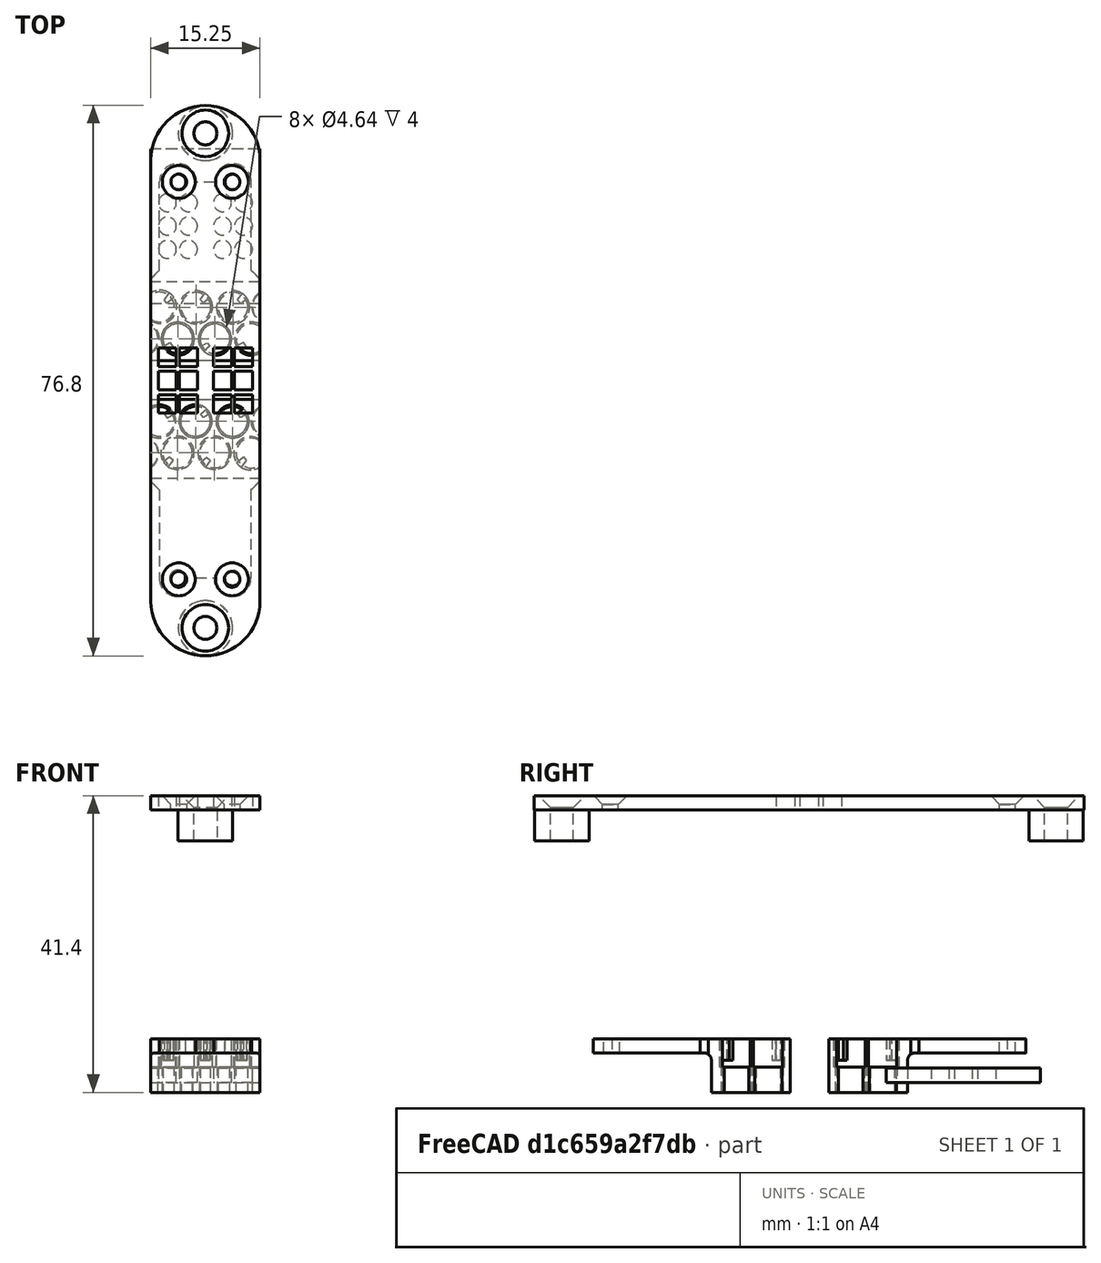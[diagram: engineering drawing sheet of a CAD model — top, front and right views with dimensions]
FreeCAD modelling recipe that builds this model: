
FCSTD DOCUMENT  (FreeCAD 0.16R6706 (Git))
Label: BrailleCell_ExplodedView
License: All rights reserved
LicenseURL: http://en.wikipedia.org/wiki/All_rights_reserved
objects: Sketcher::SketchObject×11, PartDesign::Pad×11, PartDesign::Chamfer×5, Part::MultiFuse×5, Mesh::Feature×4, Part::Box×2, Part::Cut×2, PartDesign::Fillet×2
note: 49 computed .brp shape members not serialized (recipe doc carries the construction recipe); baked Part::Feature solids carry a one-line shape summary decoded from their .brp

FEATURE [Sketcher::SketchObject] Sketch001
  sketch-geometry (12):
    g0: LineSegment StartX=0 StartY=0 StartZ=0 EndX=15.232 EndY=0 EndZ=0
    g1: LineSegment StartX=15.232 StartY=0 StartZ=0 EndX=15.232 EndY=-20 EndZ=0
    g2: LineSegment StartX=15.232 StartY=-20 StartZ=0 EndX=0 EndY=-20 EndZ=0
    g3: LineSegment StartX=0 StartY=-20 StartZ=0 EndX=0 EndY=0 EndZ=0
    g4: Circle CenterX=3.8995 CenterY=-16.9419 CenterZ=0 NormalX=0 NormalY=0 NormalZ=1 Radius=1.1
    g5: Circle CenterX=11.3325 CenterY=-16.9419 CenterZ=0 NormalX=0 NormalY=0 NormalZ=1 Radius=1.1
    g6: LineSegment StartX=0 StartY=21.56 StartZ=0 EndX=15.232 EndY=21.56 EndZ=0
    g7: LineSegment StartX=15.232 StartY=21.56 StartZ=0 EndX=15.232 EndY=41.56 EndZ=0
    g8: LineSegment StartX=15.232 StartY=41.56 StartZ=0 EndX=0 EndY=41.56 EndZ=0
    g9: LineSegment StartX=0 StartY=41.56 StartZ=0 EndX=0 EndY=21.56 EndZ=0
    g10: Circle CenterX=3.8995 CenterY=38.5019 CenterZ=0 NormalX=0 NormalY=0 NormalZ=1 Radius=1.1
    g11: Circle CenterX=11.3325 CenterY=38.5019 CenterZ=0 NormalX=0 NormalY=0 NormalZ=1 Radius=1.1
  constraints (34):
    c: Coincident(g0,g1)
    c: Coincident(g1,g2)
    c: Coincident(g2,g3)
    c: Coincident(g3,g0)
    c: Horizontal(g0)
    c: Horizontal(g2)
    c: Vertical(g1)
    c: Vertical(g3)
    c: DistanceX(g-1,g0) = 15.232
    c: DistanceY(g2,g-1) = 20
    c: DistanceY(g4,g-1) = 16.9419
    c: Radius(g4) = 1.1
    c: DistanceY(g5,g-1) = 16.9419
    c: Radius(g5) = 1.1
    c: Coincident(g6,g7)
    c: Coincident(g7,g8)
    c: Coincident(g8,g9)
    c: Coincident(g9,g6)
    c: Horizontal(g6)
    c: Horizontal(g8)
    c: Vertical(g7)
    c: Vertical(g9)
    c: PointOnObject(g6,g-2)
    c: DistanceX(g6,g6) = 15.232
    c: DistanceY(g6,g7) = 20
    c: Radius(g11) = 1.1
    c: Radius(g10) = 1.1
    c: DistanceY(g-1,g10) = 38.5019
    c: DistanceY(g-1,g11) = 38.5019
    c: DistanceX(g6,g10) = 3.8995
    c: DistanceX(g-1,g11) = 11.3325
    c: DistanceX(g-1,g4) = 3.8995
    c: DistanceX(g-1,g5) = 11.3325
    c: DistanceY(g-1,g6) = 21.56
FEATURE [Sketcher::SketchObject] Sketch002
  sketch-geometry (6):
    g0: ArcOfCircle CenterX=7.616 CenterY=41.56 CenterZ=0 NormalX=0 NormalY=0 NormalZ=1 Radius=7.616 StartAngle=0 EndAngle=3.14159
    g1: ArcOfCircle CenterX=7.616 CenterY=-20 CenterZ=0 NormalX=0 NormalY=0 NormalZ=1 Radius=7.616 StartAngle=3.14159 EndAngle=6.28319
    g2: Circle CenterX=7.616 CenterY=45.28 CenterZ=0 NormalX=0 NormalY=0 NormalZ=1 Radius=1.6
    g3: Circle CenterX=7.616 CenterY=-23.72 CenterZ=0 NormalX=0 NormalY=0 NormalZ=1 Radius=1.6
    g4: LineSegment StartX=0 StartY=-20 StartZ=0 EndX=15.232 EndY=-20 EndZ=0
    g5: LineSegment StartX=0 StartY=41.56 StartZ=0 EndX=15.232 EndY=41.56 EndZ=0
  constraints (20):
    c: DistanceY(g-1,g0) = 41.56
    c: DistanceY(g-1,g0) = 41.56
    c: DistanceY(g-1,g0) = 41.56
    c: DistanceX(g-1,g0) = 7.616
    c: DistanceY(g1,g-1) = 20
    c: DistanceX(g-1,g1) = 7.616
    c: Radius(g2) = 1.6
    c: DistanceY(g-1,g2) = 45.28
    c: DistanceX(g-1,g2) = 7.616
    c: DistanceX(g1,g3) = 7.616
    c: Radius(g3) = 1.6
    c: DistanceY(g3,g-1) = 23.72
    c: Coincident(g4,g1)
    c: Coincident(g4,g1)
    c: Horizontal(g4)
    c: Coincident(g5,g0)
    c: Coincident(g5,g0)
    c: DistanceX(g-1,g0) = 0
    c: DistanceX(g-1,g1) = 0
    c: DistanceY(g1,g1) = 0
FEATURE [PartDesign::Pad] Pad
  Length = 2
  Length2 = 100
  Sketch = -> Sketch002
  Type = 0
FEATURE [PartDesign::Pad] Pad001
  Length = 2
  Length2 = 100
  Sketch = -> Sketch001
  Type = 0
FEATURE [Sketcher::SketchObject] Sketch004
  sketch-geometry (16):
    g0: LineSegment StartX=0 StartY=0 StartZ=0 EndX=15.232 EndY=0 EndZ=0
    g1: LineSegment StartX=15.232 StartY=0 StartZ=0 EndX=15.232 EndY=21.56 EndZ=0
    g2: LineSegment StartX=15.232 StartY=21.56 StartZ=0 EndX=0 EndY=21.56 EndZ=0
    g3: LineSegment StartX=0 StartY=21.56 StartZ=0 EndX=0 EndY=0 EndZ=0
    g4: Circle CenterX=2.3099 CenterY=7.53 CenterZ=0 NormalX=0 NormalY=0 NormalZ=1 Radius=1.25
    g5: Circle CenterX=2.3099 CenterY=14.03 CenterZ=0 NormalX=0 NormalY=0 NormalZ=1 Radius=1.25
    g6: Circle CenterX=2.3099 CenterY=10.78 CenterZ=0 NormalX=0 NormalY=0 NormalZ=1 Radius=1.25
    g7: Circle CenterX=5.2399 CenterY=14.03 CenterZ=0 NormalX=0 NormalY=0 NormalZ=1 Radius=1.25
    g8: Circle CenterX=5.2399 CenterY=10.78 CenterZ=0 NormalX=0 NormalY=0 NormalZ=1 Radius=1.25
    g9: Circle CenterX=5.2399 CenterY=7.53 CenterZ=0 NormalX=0 NormalY=0 NormalZ=1 Radius=1.25
    g10: Circle CenterX=10 CenterY=14.03 CenterZ=0 NormalX=0 NormalY=0 NormalZ=1 Radius=1.25
    g11: Circle CenterX=10 CenterY=10.78 CenterZ=0 NormalX=0 NormalY=0 NormalZ=1 Radius=1.25
    g12: Circle CenterX=10 CenterY=7.53 CenterZ=0 NormalX=0 NormalY=0 NormalZ=1 Radius=1.25
    g13: Circle CenterX=12.93 CenterY=7.53 CenterZ=0 NormalX=0 NormalY=0 NormalZ=1 Radius=1.25
    g14: Circle CenterX=12.93 CenterY=10.78 CenterZ=0 NormalX=0 NormalY=0 NormalZ=1 Radius=1.25
    g15: Circle CenterX=12.93 CenterY=14.03 CenterZ=0 NormalX=0 NormalY=0 NormalZ=1 Radius=1.25
  constraints (47):
    c: Coincident(g0,g1)
    c: Coincident(g1,g2)
    c: Coincident(g2,g3)
    c: Coincident(g3,g0)
    c: Horizontal(g0)
    c: Horizontal(g2)
    c: Vertical(g1)
    c: Vertical(g3)
    c: Coincident(g0,g-1)
    c: DistanceX(g-1,g0) = 15.232
    c: DistanceY(g-1,g2) = 21.56
    c: DistanceX(g3,g4) = 2.3099
    c: Radius(g4) = 1.25
    c: DistanceY(g4,g6) = 3.25
    c: Radius(g6) = 1.25
    c: DistanceX(g4,g6) = 0
    c: DistanceX(g6,g5) = 0
    c: Radius(g5) = 1.25
    c: DistanceY(g6,g5) = 3.25
    c: DistanceY(g3,g6) = -10.78
    c: Radius(g9) = 1.25
    c: Radius(g8) = 1.25
    c: Radius(g7) = 1.25
    c: DistanceX(g8,g9) = 0
    c: DistanceX(g7,g8) = 0
    c: DistanceY(g8,g7) = 3.25
    c: DistanceY(g9,g8) = 3.25
    c: DistanceX(g4,g9) = 2.93
    c: DistanceY(g6,g8) = 0
    c: Radius(g15) = 1.25
    c: Radius(g10) = 1.25
    c: Radius(g11) = 1.25
    c: Radius(g14) = 1.25
    c: Radius(g12) = 1.25
    c: Radius(g13) = 1.25
    c: DistanceX(g13,g14) = 0
    c: DistanceX(g15,g14) = 0
    c: DistanceY(g14,g15) = 3.25
    c: DistanceY(g13,g14) = 3.25
    c: DistanceX(g12,g11) = 0
    c: DistanceX(g11,g10) = 0
    c: DistanceY(g11,g10) = 3.25
    c: DistanceY(g12,g11) = 3.25
    c: DistanceY(g13,g12) = 0
    c: DistanceY(g3,g11) = -10.78
    c: DistanceX(g3,g11) = 10
    c: DistanceX(g11,g14) = 2.93
FEATURE [PartDesign::Pad] Pad002
  Length = 2
  Length2 = 100
  Sketch = -> Sketch004
  Type = 0
FEATURE [PartDesign::Chamfer] Chamfer
  Base = -> Pad [Edge8]
  Size = 1.65
FEATURE [PartDesign::Chamfer] Chamfer002
  Base = -> Pad001 [Edge35,Edge32,Edge17,Edge14]
  Size = 1.2
FEATURE [PartDesign::Chamfer] Chamfer003
  Base = -> Chamfer [Edge19]
  Size = 1.65
FEATURE [Sketcher::SketchObject] Sketch005
  sketch-geometry (52):
    g0: LineSegment StartX=0 StartY=0 StartZ=0 EndX=15.232 EndY=0 EndZ=0
    g1: LineSegment StartX=15.232 StartY=0 StartZ=0 EndX=15.232 EndY=21.56 EndZ=0
    g2: LineSegment StartX=15.232 StartY=21.56 StartZ=0 EndX=0 EndY=21.56 EndZ=0
    g3: LineSegment StartX=0 StartY=21.56 StartZ=0 EndX=0 EndY=0 EndZ=0
    g4: LineSegment StartX=1.0599 StartY=12.08 StartZ=0 EndX=3.5599 EndY=12.08 EndZ=0
    g5: LineSegment StartX=3.5599 StartY=12.08 StartZ=0 EndX=3.5599 EndY=9.48 EndZ=0
    g6: LineSegment StartX=3.5599 StartY=9.48 StartZ=0 EndX=1.0599 EndY=9.48 EndZ=0
    g7: LineSegment StartX=1.0599 StartY=9.48 StartZ=0 EndX=1.0599 EndY=12.08 EndZ=0
    g8: LineSegment StartX=1.0599 StartY=15.33 StartZ=0 EndX=3.5599 EndY=15.33 EndZ=0
    g9: LineSegment StartX=3.5599 StartY=15.33 StartZ=0 EndX=3.5599 EndY=12.73 EndZ=0
    g10: LineSegment StartX=3.5599 StartY=12.73 StartZ=0 EndX=1.0599 EndY=12.73 EndZ=0
    g11: LineSegment StartX=1.0599 StartY=12.73 StartZ=0 EndX=1.0599 EndY=15.33 EndZ=0
    g12: LineSegment StartX=1.0599 StartY=8.83 StartZ=0 EndX=3.5599 EndY=8.83 EndZ=0
    g13: LineSegment StartX=3.5599 StartY=8.83 StartZ=0 EndX=3.5599 EndY=6.23 EndZ=0
    g14: LineSegment StartX=3.5599 StartY=6.23 StartZ=0 EndX=1.0599 EndY=6.23 EndZ=0
    g15: LineSegment StartX=1.0599 StartY=6.23 StartZ=0 EndX=1.0599 EndY=8.83 EndZ=0
    g16: LineSegment StartX=3.9899 StartY=15.33 StartZ=0 EndX=6.4899 EndY=15.33 EndZ=0
    g17: LineSegment StartX=6.4899 StartY=15.33 StartZ=0 EndX=6.4899 EndY=12.73 EndZ=0
    g18: LineSegment StartX=6.4899 StartY=12.73 StartZ=0 EndX=3.9899 EndY=12.73 EndZ=0
    g19: LineSegment StartX=3.9899 StartY=12.73 StartZ=0 EndX=3.9899 EndY=15.33 EndZ=0
    g20: LineSegment StartX=3.9899 StartY=12.08 StartZ=0 EndX=6.4899 EndY=12.08 EndZ=0
    g21: LineSegment StartX=6.4899 StartY=12.08 StartZ=0 EndX=6.4899 EndY=9.48 EndZ=0
    g22: LineSegment StartX=6.4899 StartY=9.48 StartZ=0 EndX=3.9899 EndY=9.48 EndZ=0
    g23: LineSegment StartX=3.9899 StartY=9.48 StartZ=0 EndX=3.9899 EndY=12.08 EndZ=0
    g24: LineSegment StartX=3.9899 StartY=8.83 StartZ=0 EndX=6.4899 EndY=8.83 EndZ=0
    g25: LineSegment StartX=6.4899 StartY=8.83 StartZ=0 EndX=6.4899 EndY=6.23 EndZ=0
    g26: LineSegment StartX=6.4899 StartY=6.23 StartZ=0 EndX=3.9899 EndY=6.23 EndZ=0
    g27: LineSegment StartX=3.9899 StartY=6.23 StartZ=0 EndX=3.9899 EndY=8.83 EndZ=0
    g28: LineSegment StartX=8.75 StartY=15.33 StartZ=0 EndX=11.25 EndY=15.33 EndZ=0
    g29: LineSegment StartX=11.25 StartY=15.33 StartZ=0 EndX=11.25 EndY=12.73 EndZ=0
    g30: LineSegment StartX=11.25 StartY=12.73 StartZ=0 EndX=8.75 EndY=12.73 EndZ=0
    g31: LineSegment StartX=8.75 StartY=12.73 StartZ=0 EndX=8.75 EndY=15.33 EndZ=0
    g32: LineSegment StartX=11.68 StartY=15.33 StartZ=0 EndX=14.18 EndY=15.33 EndZ=0
    g33: LineSegment StartX=14.18 StartY=15.33 StartZ=0 EndX=14.18 EndY=12.73 EndZ=0
    g34: LineSegment StartX=14.18 StartY=12.73 StartZ=0 EndX=11.68 EndY=12.73 EndZ=0
    g35: LineSegment StartX=11.68 StartY=12.73 StartZ=0 EndX=11.68 EndY=15.33 EndZ=0
    g36: LineSegment StartX=8.75 StartY=12.08 StartZ=0 EndX=11.25 EndY=12.08 EndZ=0
    g37: LineSegment StartX=11.25 StartY=12.08 StartZ=0 EndX=11.25 EndY=9.48 EndZ=0
    g38: LineSegment StartX=11.25 StartY=9.48 StartZ=0 EndX=8.75 EndY=9.48 EndZ=0
    g39: LineSegment StartX=8.75 StartY=9.48 StartZ=0 EndX=8.75 EndY=12.08 EndZ=0
    g40: LineSegment StartX=11.68 StartY=12.08 StartZ=0 EndX=14.18 EndY=12.08 EndZ=0
    g41: LineSegment StartX=14.18 StartY=12.08 StartZ=0 EndX=14.18 EndY=9.48 EndZ=0
    g42: LineSegment StartX=14.18 StartY=9.48 StartZ=0 EndX=11.68 EndY=9.48 EndZ=0
    g43: LineSegment StartX=11.68 StartY=9.48 StartZ=0 EndX=11.68 EndY=12.08 EndZ=0
    g44: LineSegment StartX=8.75 StartY=8.83 StartZ=0 EndX=11.25 EndY=8.83 EndZ=0
    g45: LineSegment StartX=11.25 StartY=8.83 StartZ=0 EndX=11.25 EndY=6.23 EndZ=0
    g46: LineSegment StartX=11.25 StartY=6.23 StartZ=0 EndX=8.75 EndY=6.23 EndZ=0
    g47: LineSegment StartX=8.75 StartY=6.23 StartZ=0 EndX=8.75 EndY=8.83 EndZ=0
    g48: LineSegment StartX=11.68 StartY=8.83 StartZ=0 EndX=14.18 EndY=8.83 EndZ=0
    g49: LineSegment StartX=14.18 StartY=8.83 StartZ=0 EndX=14.18 EndY=6.23 EndZ=0
    g50: LineSegment StartX=14.18 StartY=6.23 StartZ=0 EndX=11.68 EndY=6.23 EndZ=0
    g51: LineSegment StartX=11.68 StartY=6.23 StartZ=0 EndX=11.68 EndY=8.83 EndZ=0
  constraints (155):
    c: Coincident(g0,g1)
    c: Coincident(g1,g2)
    c: Coincident(g2,g3)
    c: Coincident(g3,g0)
    c: Horizontal(g0)
    c: Horizontal(g2)
    c: Vertical(g1)
    c: Vertical(g3)
    c: Coincident(g0,g-1)
    c: DistanceX(g-1,g0) = 15.232
    c: DistanceY(g-1,g2) = 21.56
    c: Coincident(g4,g5)
    c: Coincident(g5,g6)
    c: Coincident(g6,g7)
    c: Coincident(g7,g4)
    c: Horizontal(g4)
    c: Horizontal(g6)
    c: Vertical(g5)
    c: Vertical(g7)
    c: Coincident(g8,g9)
    c: Coincident(g9,g10)
    c: Coincident(g10,g11)
    c: Coincident(g11,g8)
    c: Horizontal(g8)
    c: Horizontal(g10)
    c: Vertical(g9)
    c: Vertical(g11)
    c: Coincident(g12,g13)
    c: Coincident(g13,g14)
    c: Coincident(g14,g15)
    c: Coincident(g15,g12)
    c: Horizontal(g12)
    c: Horizontal(g14)
    c: Vertical(g13)
    c: Vertical(g15)
    c: Coincident(g16,g17)
    c: Coincident(g17,g18)
    c: Coincident(g18,g19)
    c: Coincident(g19,g16)
    c: Horizontal(g16)
    c: Horizontal(g18)
    c: Vertical(g17)
    c: Vertical(g19)
    c: Coincident(g20,g21)
    c: Coincident(g21,g22)
    c: Coincident(g22,g23)
    c: Coincident(g23,g20)
    c: Horizontal(g20)
    c: Horizontal(g22)
    c: Vertical(g21)
    c: Vertical(g23)
    c: Coincident(g24,g25)
    c: Coincident(g25,g26)
    c: Coincident(g26,g27)
    c: Coincident(g27,g24)
    c: Horizontal(g24)
    c: Horizontal(g26)
    c: Vertical(g25)
    c: Vertical(g27)
    c: DistanceY(g6,g4) = 2.6
    c: DistanceY(g10,g8) = 2.6
    c: DistanceY(g14,g12) = 2.6
    c: DistanceY(g-1,g6) = 9.48
    c: DistanceY(g22,g20) = 2.6
    c: DistanceY(g18,g16) = 2.6
    c: DistanceY(g26,g24) = 2.6
    c: DistanceY(g4,g10) = 0.65
    c: DistanceY(g12,g6) = 0.65
    c: DistanceY(g24,g22) = 0.65
    c: DistanceY(g20,g18) = 0.65
    c: DistanceX(g6,g5) = 2.5
    c: DistanceX(g14,g13) = 2.5
    c: DistanceX(g10,g4) = 0
    c: DistanceX(g6,g12) = 0
    c: DistanceX(g10,g9) = 2.5
    c: DistanceX(g20,g18) = 0
    c: DistanceX(g22,g24) = 0
    c: DistanceX(g22,g21) = 2.5
    c: DistanceX(g26,g25) = 2.5
    c: DistanceX(g18,g17) = 2.5
    c: DistanceX(g5,g22) = 0.43
    c: DistanceX(g-1,g6) = 1.0599
    c: Coincident(g28,g29)
    c: Coincident(g29,g30)
    c: Coincident(g30,g31)
    c: Coincident(g31,g28)
    c: Horizontal(g28)
    c: Horizontal(g30)
    c: Vertical(g29)
    c: Vertical(g31)
    c: Coincident(g32,g33)
    c: Coincident(g33,g34)
    c: Coincident(g34,g35)
    c: Coincident(g35,g32)
    c: Horizontal(g32)
    c: Horizontal(g34)
    c: Vertical(g33)
    c: Vertical(g35)
    c: Coincident(g36,g37)
    c: Coincident(g37,g38)
    c: Coincident(g38,g39)
    c: Coincident(g39,g36)
    c: Horizontal(g36)
    c: Horizontal(g38)
    c: Vertical(g37)
    c: Vertical(g39)
    c: Coincident(g40,g41)
    c: Coincident(g41,g42)
    c: Coincident(g42,g43)
    c: Coincident(g43,g40)
    c: Horizontal(g40)
    c: Horizontal(g42)
    c: Vertical(g41)
    c: Vertical(g43)
    c: Coincident(g44,g45)
    c: Coincident(g45,g46)
    c: Coincident(g46,g47)
    c: Coincident(g47,g44)
    c: Horizontal(g44)
    c: Horizontal(g46)
    c: Vertical(g45)
    c: Vertical(g47)
    c: Coincident(g48,g49)
    c: Coincident(g49,g50)
    c: Coincident(g50,g51)
    c: Coincident(g51,g48)
    c: Horizontal(g48)
    c: Horizontal(g50)
    c: Vertical(g49)
    c: Vertical(g51)
    c: DistanceX(g-1,g38) = 8.75
    c: DistanceX(g36,g36) = 2.5
    c: DistanceX(g30,g29) = 2.5
    c: DistanceX(g44,g44) = 2.5
    c: DistanceX(g40,g40) = 2.5
    c: DistanceX(g34,g33) = 2.5
    c: DistanceX(g50,g49) = 2.5
    c: DistanceY(g46,g44) = 2.6
    c: DistanceY(g50,g48) = 2.6
    c: DistanceY(g42,g40) = 2.6
    c: DistanceY(g30,g28) = 2.6
    c: DistanceY(g34,g32) = 2.6
    c: DistanceY(g38,g36) = 2.6
    c: DistanceX(g38,g44) = 0
    c: DistanceX(g30,g36) = 0
    c: DistanceX(g34,g40) = 0
    c: DistanceX(g42,g48) = 0
    c: DistanceY(g48,g42) = 0.65
    c: DistanceY(g44,g38) = 0.65
    c: DistanceY(g40,g34) = 0.65
    c: DistanceY(g36,g30) = 0.65
    c: DistanceY(g42,g37) = 0
    c: DistanceX(g37,g42) = 0.43
    c: DistanceY(g-1,g38) = 9.48
    c: DistanceY(g22,g5) = 0
FEATURE [PartDesign::Pad] Pad003
  Length = 2
  Length2 = 100
  Sketch = -> Sketch005
  Type = 0
FEATURE [Sketcher::SketchObject] Sketch
  Placement = pos=(0,0,2) rot=(0,0,1;0rad)
  sketch-geometry (4):
    g0: Circle CenterX=7.616 CenterY=45.28 CenterZ=0 NormalX=0 NormalY=0 NormalZ=1 Radius=3.8
    g1: Circle CenterX=7.616 CenterY=45.28 CenterZ=0 NormalX=0 NormalY=0 NormalZ=1 Radius=1.6
    g2: Circle CenterX=7.616 CenterY=-23.72 CenterZ=0 NormalX=0 NormalY=0 NormalZ=1 Radius=3.8
    g3: Circle CenterX=7.616 CenterY=-23.72 CenterZ=0 NormalX=0 NormalY=0 NormalZ=1 Radius=1.6
  constraints (10):
    c: Radius(g0) = 3.8
    c: Coincident(g1,g0)
    c: Radius(g1) = 1.6
    c: DistanceX(g-1,g0) = 7.616
    c: DistanceY(g-1,g0) = 45.28
    c: Coincident(g3,g2)
    c: Radius(g2) = 3.8
    c: Radius(g3) = 1.6
    c: DistanceX(g-1,g2) = 7.616
    c: DistanceY(g2,g-1) = 23.72
FEATURE [PartDesign::Pad] Pad004
  Length = 4.3
  Length2 = 100
  Placement = pos=(0,0,2) rot=(0,0,1;0rad)
  Sketch = -> Sketch
  Type = 0
FEATURE [Mesh::Feature] Pins_3  label="Pins 3"
  Placement = pos=(-0.8,-41,26.5) rot=(0,0,1;0rad)
FEATURE [Part::MultiFuse] Fusion
  Placement = pos=(0,0,40) rot=(1,0,0;3.14159rad)
  Shapes = -> [Chamfer002,Chamfer003,Pad003,Pad004]
FEATURE [Mesh::Feature] Pins_3001  label="Pins 004"
  Placement = pos=(16,19.5,26.5) rot=(0,0,1;3.14159rad)
FEATURE [Mesh::Feature] Lever_Old_Design_1_2  label="Lever Old Design 1.2"
  Placement = pos=(2.2,-19.6,16.2) rot=(0,-1,0;1.5708rad)
FEATURE [Mesh::Feature] Lever_Old_Design_1_2001  label="Lever Old Design 1.003"
  Placement = pos=(13.05,-1.9,15.2) rot=(0.707107,0,0.707107;3.14159rad)
FEATURE [Sketcher::SketchObject] Sketch006
  sketch-geometry (24):
    g0: LineSegment StartX=1.16719 StartY=12.6074 StartZ=0 EndX=1.16719 EndY=24.9153 EndZ=0
    g1: LineSegment StartX=6.28798 StartY=24.9169 StartZ=0 EndX=8.82572 EndY=24.9169 EndZ=0
    g2: LineSegment StartX=13.9682 StartY=12.5724 StartZ=0 EndX=13.9682 EndY=24.9342 EndZ=0
    g3: ArcOfCircle CenterX=3.72758 CenterY=24.9165 CenterZ=0 NormalX=0 NormalY=0 NormalZ=1 Radius=2.56039 StartAngle=0.000160774 EndAngle=3.14208
    g4: ArcOfCircle CenterX=11.397 CenterY=24.9235 CenterZ=0 NormalX=0 NormalY=0 NormalZ=1 Radius=2.57125 StartAngle=0.00415218 EndAngle=3.14415
    g5: Circle CenterX=3.72758 CenterY=24.9165 CenterZ=0 NormalX=0 NormalY=0 NormalZ=1 Radius=1.1
    g6: Circle CenterX=11.392 CenterY=24.9235 CenterZ=0 NormalX=0 NormalY=0 NormalZ=1 Radius=1.1
    g7: LineSegment StartX=0 StartY=0 StartZ=0 EndX=15.2 EndY=0 EndZ=0
    g8: LineSegment StartX=15.2 StartY=12.5724 StartZ=0 EndX=13.9682 EndY=12.5724 EndZ=0
    g9: LineSegment StartX=0 StartY=12.6074 StartZ=0 EndX=1.16719 EndY=12.6074 EndZ=0
    g10: Circle CenterX=3.71 CenterY=7.45 CenterZ=0 NormalX=0 NormalY=0 NormalZ=1 Radius=2.32
    g11: Circle CenterX=8.8865 CenterY=7.45 CenterZ=0 NormalX=0 NormalY=0 NormalZ=1 Radius=2.32
    g12: Circle CenterX=11.4178 CenterY=3.06406 CenterZ=0 NormalX=0 NormalY=0 NormalZ=1 Radius=2.32
    g13: Circle CenterX=6.22788 CenterY=3.05007 CenterZ=0 NormalX=0 NormalY=0 NormalZ=1 Radius=2.32
    g14: ArcOfCircle CenterX=-1.2323 CenterY=7.51766 CenterZ=0 NormalX=0 NormalY=0 NormalZ=1 Radius=2.32 StartAngle=5.27236 EndAngle=7.29401
    g15: ArcOfCircle CenterX=1.16612 CenterY=3.07188 CenterZ=0 NormalX=0 NormalY=0 NormalZ=1 Radius=2.32 StartAngle=4.18574 EndAngle=8.38063
    g16: ArcOfCircle CenterX=13.8979 CenterY=7.52681 CenterZ=0 NormalX=0 NormalY=0 NormalZ=1 Radius=2.32 StartAngle=0.974907 EndAngle=5.30828
    g17: LineSegment StartX=15.2 StartY=9.44695 StartZ=0 EndX=15.2 EndY=12.5724 EndZ=0
    g18: LineSegment StartX=15.2 StartY=5.60666 StartZ=0 EndX=15.2 EndY=5.12562 EndZ=0
    g19: LineSegment StartX=15.2 StartY=1.04863 StartZ=0 EndX=15.2 EndY=0 EndZ=0
    g20: LineSegment StartX=0 StartY=0 StartZ=0 EndX=0 EndY=1.06625 EndZ=0
    g21: LineSegment StartX=0 StartY=5.07751 StartZ=0 EndX=0 EndY=5.55199 EndZ=0
    g22: LineSegment StartX=0 StartY=9.48333 StartZ=0 EndX=0 EndY=12.6074 EndZ=0
    g23: ArcOfCircle CenterX=16.3077 CenterY=3.08713 CenterZ=0 NormalX=0 NormalY=0 NormalZ=1 Radius=2.32 StartAngle=2.06854 EndAngle=4.21464
  constraints (50):
    c: Vertical(g0)
    c: Horizontal(g1)
    c: Vertical(g2)
    c: Coincident(g3,g0)
    c: Coincident(g3,g1)
    c: Coincident(g4,g1)
    c: Coincident(g4,g2)
    c: Coincident(g5,g3)
    c: Horizontal(g7)
    c: Coincident(g7,g-1)
    c: Coincident(g8,g2)
    c: Horizontal(g8)
    c: Coincident(g9,g0)
    c: Horizontal(g9)
    c: Radius(g10) = 2.32
    c: DistanceY(g-1,g10) = 7.45
    c: DistanceX(g-1,g10) = 3.71
    c: Radius(g11) = 2.32
    c: Radius(g12) = 2.32
    c: Radius(g13) = 2.32
    c: Radius(g15) = 2.32
    c: Radius(g16) = 2.32
    c: DistanceY(g-1,g11) = 7.45
    c: Coincident(g17,g16)
    c: Coincident(g17,g8)
    c: Vertical(g17)
    c: Coincident(g18,g16)
    c: Vertical(g18)
    c: Coincident(g19,g7)
    c: Vertical(g19)
    c: Coincident(g20,g-1)
    c: Coincident(g20,g15)
    c: Vertical(g20)
    c: Coincident(g21,g15)
    c: Coincident(g21,g14)
    c: Vertical(g21)
    c: Coincident(g22,g14)
    c: Coincident(g22,g9)
    c: Vertical(g22)
    c: DistanceX(g9,g8) = 15.2
    c: DistanceX(g14,g16) = 15.2
    c: DistanceX(g-1,g7) = 15.2
    c: Coincident(g23,g18)
    c: Coincident(g23,g19)
    c: DistanceX(g-1,g14) = 0
    c: DistanceX(g-1,g15) = 0
    c: Radius(g14) = 2.32
    c: Radius(g23) = 2.32
    c: Radius(g5) = 1.1
    c: Radius(g6) = 1.1
FEATURE [PartDesign::Pad] Pad005
  Length = 4
  Length2 = 100
  Sketch = -> Sketch006
  Type = 0
FEATURE [Sketcher::SketchObject] Sketch007
  Placement = pos=(0,0,4) rot=(0,0,1;0rad)
  sketch-geometry (16):
    g0: LineSegment StartX=0 StartY=0 StartZ=0 EndX=15.2 EndY=0 EndZ=0
    g1: Circle CenterX=3.71 CenterY=7.45 CenterZ=0 NormalX=0 NormalY=0 NormalZ=1 Radius=2.08
    g2: Circle CenterX=8.8865 CenterY=7.45 CenterZ=0 NormalX=0 NormalY=0 NormalZ=1 Radius=2.08
    g3: Circle CenterX=11.4178 CenterY=3.06406 CenterZ=0 NormalX=0 NormalY=0 NormalZ=1 Radius=2.08
    g4: Circle CenterX=6.22788 CenterY=3.05007 CenterZ=0 NormalX=0 NormalY=0 NormalZ=1 Radius=2.08
    g5: ArcOfCircle CenterX=-1.29213 CenterY=7.49891 CenterZ=0 NormalX=0 NormalY=0 NormalZ=1 Radius=2.27568 StartAngle=5.31622 EndAngle=7.25015
    g6: ArcOfCircle CenterX=1.20105 CenterY=3.06417 CenterZ=0 NormalX=0 NormalY=0 NormalZ=1 Radius=2.08 StartAngle=4.09681 EndAngle=8.46956
    g7: ArcOfCircle CenterX=13.9805 CenterY=7.48824 CenterZ=0 NormalX=0 NormalY=0 NormalZ=1 Radius=2.08 StartAngle=0.944332 EndAngle=5.33885
    g8: LineSegment StartX=15.2 StartY=5.80322 StartZ=0 EndX=15.2 EndY=4.94257 EndZ=0
    g9: LineSegment StartX=15.2 StartY=1.15374 StartZ=0 EndX=15.2 EndY=0 EndZ=0
    g10: LineSegment StartX=0 StartY=0 StartZ=0 EndX=0 EndY=1.36598 EndZ=0
    g11: LineSegment StartX=0 StartY=4.76237 StartZ=0 EndX=0 EndY=5.62564 EndZ=0
    g12: ArcOfCircle CenterX=16.4748 CenterY=3.04816 CenterZ=0 NormalX=0 NormalY=0 NormalZ=1 Radius=2.28338 StartAngle=2.1631 EndAngle=4.12008
    g13: LineSegment StartX=0 StartY=11 StartZ=0 EndX=15.2 EndY=11 EndZ=0
    g14: LineSegment StartX=15.2 StartY=9.17326 StartZ=0 EndX=15.2 EndY=11 EndZ=0
    g15: LineSegment StartX=0 StartY=9.37218 StartZ=0 EndX=0 EndY=11 EndZ=0
  constraints (36):
    c: Horizontal(g0)
    c: Coincident(g0,g-1)
    c: Radius(g1) = 2.08
    c: DistanceY(g-1,g1) = 7.45
    c: DistanceX(g-1,g1) = 3.71
    c: Radius(g2) = 2.08
    c: Radius(g3) = 2.08
    c: Radius(g4) = 2.08
    c: Radius(g6) = 2.08
    c: Radius(g7) = 2.08
    c: DistanceY(g-1,g2) = 7.45
    c: Coincident(g8,g7)
    c: Vertical(g8)
    c: Coincident(g9,g0)
    c: Vertical(g9)
    c: Coincident(g10,g-1)
    c: Coincident(g10,g6)
    c: Vertical(g10)
    c: Coincident(g11,g6)
    c: Coincident(g11,g5)
    c: Vertical(g11)
    c: DistanceX(g5,g7) = 15.2
    c: DistanceX(g-1,g0) = 15.2
    c: Coincident(g12,g8)
    c: Coincident(g12,g9)
    c: DistanceX(g-1,g5) = 0
    c: DistanceX(g-1,g6) = 0
    c: Horizontal(g13)
    c: Coincident(g14,g7)
    c: Coincident(g14,g13)
    c: Vertical(g14)
    c: DistanceY(g-1,g13) = 11
    c: DistanceX(g13,g-1) = 0
    c: Coincident(g15,g5)
    c: Coincident(g15,g13)
    c: DistanceX(g13,g13) = 15.2
FEATURE [PartDesign::Pad] Pad006
  Length = 3.5
  Length2 = 100
  Placement = pos=(0,0,4) rot=(0,0,1;0rad)
  Sketch = -> Sketch007
  Type = 0
FEATURE [Sketcher::SketchObject] Sketch003
  sketch-geometry (24):
    g0: LineSegment StartX=2.37867 StartY=9.53855 StartZ=0 EndX=3.14154 EndY=8.48461 EndZ=0
    g1: LineSegment StartX=3.14154 StartY=8.48461 StartZ=0 EndX=2.60525 EndY=8.03091 EndZ=0
    g2: LineSegment StartX=2.60525 StartY=8.03091 StartZ=0 EndX=1.60386 EndY=8.87946 EndZ=0
    g3: LineSegment StartX=2.37867 StartY=9.53855 StartZ=0 EndX=1.60386 EndY=8.87946 EndZ=0
    g4: LineSegment StartX=6.78436 StartY=8.94076 StartZ=0 EndX=7.81191 EndY=8.04644 EndZ=0
    g5: LineSegment StartX=7.81191 StartY=8.04644 StartZ=0 EndX=8.27871 EndY=8.4965 EndZ=0
    g6: LineSegment StartX=8.27871 StartY=8.4965 StartZ=0 EndX=7.51318 EndY=9.56846 EndZ=0
    g7: LineSegment StartX=7.51318 StartY=9.56846 StartZ=0 EndX=6.78436 EndY=8.94076 EndZ=0
    g8: LineSegment StartX=11.6397 StartY=9.07747 StartZ=0 EndX=12.905 EndY=8.01886 EndZ=0
    g9: LineSegment StartX=12.905 StartY=8.01886 StartZ=0 EndX=13.2996 EndY=8.47427 EndZ=0
    g10: LineSegment StartX=13.2996 StartY=8.47427 StartZ=0 EndX=12.401 EndY=9.69575 EndZ=0
    g11: LineSegment StartX=12.401 StartY=9.69575 StartZ=0 EndX=11.6397 EndY=9.07747 EndZ=0
    g12: LineSegment StartX=12.1046 StartY=1.97636 StartZ=0 EndX=13.3056 EndY=0.90266 EndZ=0
    g13: LineSegment StartX=13.3056 StartY=0.90266 StartZ=0 EndX=13.8986 EndY=1.72895 EndZ=0
    g14: LineSegment StartX=13.8986 StartY=1.72895 StartZ=0 EndX=12.5452 EndY=2.53763 EndZ=0
    g15: LineSegment StartX=12.5452 StartY=2.53763 StartZ=0 EndX=12.1046 EndY=1.97636 EndZ=0
    g16: LineSegment StartX=8.70009 StartY=1.7485 StartZ=0 EndX=7.31743 EndY=2.50872 EndZ=0
    g17: LineSegment StartX=7.31743 StartY=2.50872 StartZ=0 EndX=6.93042 EndY=2.02516 EndZ=0
    g18: LineSegment StartX=6.93042 StartY=2.02516 StartZ=0 EndX=8.13703 EndY=1.0298 EndZ=0
    g19: LineSegment StartX=8.13703 StartY=1.0298 StartZ=0 EndX=8.70009 EndY=1.7485 EndZ=0
    g20: LineSegment StartX=2.27306 StartY=2.56746 StartZ=0 EndX=3.50885 EndY=1.8824 EndZ=0
    g21: LineSegment StartX=3.50885 StartY=1.8824 StartZ=0 EndX=2.89778 EndY=1.21181 EndZ=0
    g22: LineSegment StartX=2.89778 StartY=1.21181 StartZ=0 EndX=1.89388 EndY=2.05588 EndZ=0
    g23: LineSegment StartX=1.89388 StartY=2.05588 StartZ=0 EndX=2.27306 EndY=2.56746 EndZ=0
  constraints (24):
    c: Coincident(g1,g0)
    c: Coincident(g2,g1)
    c: Coincident(g3,g0)
    c: Coincident(g3,g2)
    c: Coincident(g4,g5)
    c: Coincident(g5,g6)
    c: Coincident(g6,g7)
    c: Coincident(g7,g4)
    c: Coincident(g8,g9)
    c: Coincident(g9,g10)
    c: Coincident(g10,g11)
    c: Coincident(g11,g8)
    c: Coincident(g12,g13)
    c: Coincident(g13,g14)
    c: Coincident(g14,g15)
    c: Coincident(g15,g12)
    c: Coincident(g16,g17)
    c: Coincident(g17,g18)
    c: Coincident(g18,g19)
    c: Coincident(g19,g16)
    c: Coincident(g20,g21)
    c: Coincident(g21,g22)
    c: Coincident(g22,g23)
    c: Coincident(g23,g20)
FEATURE [PartDesign::Pad] Pad007
  Length = 3
  Length2 = 100
  Sketch = -> Sketch003
  Type = 0
FEATURE [PartDesign::Chamfer] Chamfer004
  Base = -> Pad005 [Edge14,Edge35]
  Size = 1.16
FEATURE [Part::MultiFuse] Fusion001
  Shapes = -> [Chamfer004,Pad007,Pad006]
FEATURE [Part::Box] Box  label="Würfel"
  Height = 10
  Length = 15.2
  Placement = pos=(0,11,2) rot=(0,0,1;0rad)
  Width = 18
FEATURE [Part::Cut] Cut
  Base = -> Fusion001
  Tool = -> Box
FEATURE [PartDesign::Fillet] Fillet
  Base = -> Cut [Edge80]
  Radius = 1
FEATURE [Sketcher::SketchObject] Sketch008
  sketch-geometry (24):
    g0: LineSegment StartX=1.16719 StartY=12.6074 StartZ=0 EndX=1.16719 EndY=24.9153 EndZ=0
    g1: LineSegment StartX=6.28798 StartY=24.9169 StartZ=0 EndX=8.82572 EndY=24.9169 EndZ=0
    g2: LineSegment StartX=13.9682 StartY=12.5724 StartZ=0 EndX=13.9682 EndY=24.9342 EndZ=0
    g3: ArcOfCircle CenterX=3.72758 CenterY=24.9165 CenterZ=0 NormalX=0 NormalY=0 NormalZ=1 Radius=2.56039 StartAngle=0.000160774 EndAngle=3.14208
    g4: ArcOfCircle CenterX=11.397 CenterY=24.9235 CenterZ=0 NormalX=0 NormalY=0 NormalZ=1 Radius=2.57125 StartAngle=0.00415218 EndAngle=3.14415
    g5: Circle CenterX=3.72758 CenterY=24.9165 CenterZ=0 NormalX=0 NormalY=0 NormalZ=1 Radius=1.1
    g6: Circle CenterX=11.392 CenterY=24.9235 CenterZ=0 NormalX=0 NormalY=0 NormalZ=1 Radius=1.1
    g7: LineSegment StartX=0 StartY=0 StartZ=0 EndX=15.2 EndY=0 EndZ=0
    g8: LineSegment StartX=15.2 StartY=12.5724 StartZ=0 EndX=13.9682 EndY=12.5724 EndZ=0
    g9: LineSegment StartX=0 StartY=12.6074 StartZ=0 EndX=1.16719 EndY=12.6074 EndZ=0
    g10: Circle CenterX=3.71 CenterY=7.45 CenterZ=0 NormalX=0 NormalY=0 NormalZ=1 Radius=2.32
    g11: Circle CenterX=8.8865 CenterY=7.45 CenterZ=0 NormalX=0 NormalY=0 NormalZ=1 Radius=2.32
    g12: Circle CenterX=11.4178 CenterY=3.06406 CenterZ=0 NormalX=0 NormalY=0 NormalZ=1 Radius=2.32
    g13: Circle CenterX=6.22788 CenterY=3.05007 CenterZ=0 NormalX=0 NormalY=0 NormalZ=1 Radius=2.32
    g14: ArcOfCircle CenterX=-1.2323 CenterY=7.51766 CenterZ=0 NormalX=0 NormalY=0 NormalZ=1 Radius=2.32 StartAngle=5.27236 EndAngle=7.29401
    g15: ArcOfCircle CenterX=1.16612 CenterY=3.07188 CenterZ=0 NormalX=0 NormalY=0 NormalZ=1 Radius=2.32 StartAngle=4.18574 EndAngle=8.38063
    g16: ArcOfCircle CenterX=13.8979 CenterY=7.52681 CenterZ=0 NormalX=0 NormalY=0 NormalZ=1 Radius=2.32 StartAngle=0.974907 EndAngle=5.30828
    g17: LineSegment StartX=15.2 StartY=9.44695 StartZ=0 EndX=15.2 EndY=12.5724 EndZ=0
    g18: LineSegment StartX=15.2 StartY=5.60666 StartZ=0 EndX=15.2 EndY=5.12562 EndZ=0
    g19: LineSegment StartX=15.2 StartY=1.04863 StartZ=0 EndX=15.2 EndY=0 EndZ=0
    g20: LineSegment StartX=0 StartY=0 StartZ=0 EndX=0 EndY=1.06625 EndZ=0
    g21: LineSegment StartX=0 StartY=5.07751 StartZ=0 EndX=0 EndY=5.55199 EndZ=0
    g22: LineSegment StartX=0 StartY=9.48333 StartZ=0 EndX=0 EndY=12.6074 EndZ=0
    g23: ArcOfCircle CenterX=16.3077 CenterY=3.08713 CenterZ=0 NormalX=0 NormalY=0 NormalZ=1 Radius=2.32 StartAngle=2.06854 EndAngle=4.21464
  constraints (50):
    c: Vertical(g0)
    c: Horizontal(g1)
    c: Vertical(g2)
    c: Coincident(g3,g0)
    c: Coincident(g3,g1)
    c: Coincident(g4,g1)
    c: Coincident(g4,g2)
    c: Coincident(g5,g3)
    c: Horizontal(g7)
    c: Coincident(g7,g-1)
    c: Coincident(g8,g2)
    c: Horizontal(g8)
    c: Coincident(g9,g0)
    c: Horizontal(g9)
    c: Radius(g10) = 2.32
    c: DistanceY(g-1,g10) = 7.45
    c: DistanceX(g-1,g10) = 3.71
    c: Radius(g11) = 2.32
    c: Radius(g12) = 2.32
    c: Radius(g13) = 2.32
    c: Radius(g15) = 2.32
    c: Radius(g16) = 2.32
    c: DistanceY(g-1,g11) = 7.45
    c: Coincident(g17,g16)
    c: Coincident(g17,g8)
    c: Vertical(g17)
    c: Coincident(g18,g16)
    c: Vertical(g18)
    c: Coincident(g19,g7)
    c: Vertical(g19)
    c: Coincident(g20,g-1)
    c: Coincident(g20,g15)
    c: Vertical(g20)
    c: Coincident(g21,g15)
    c: Coincident(g21,g14)
    c: Vertical(g21)
    c: Coincident(g22,g14)
    c: Coincident(g22,g9)
    c: Vertical(g22)
    c: DistanceX(g9,g8) = 15.2
    c: DistanceX(g14,g16) = 15.2
    c: DistanceX(g-1,g7) = 15.2
    c: Coincident(g23,g18)
    c: Coincident(g23,g19)
    c: DistanceX(g-1,g14) = 0
    c: DistanceX(g-1,g15) = 0
    c: Radius(g14) = 2.32
    c: Radius(g23) = 2.32
    c: Radius(g5) = 1.1
    c: Radius(g6) = 1.1
FEATURE [PartDesign::Pad] Pad008
  Length = 4
  Length2 = 100
  Sketch = -> Sketch008
  Type = 0
FEATURE [Sketcher::SketchObject] Sketch009
  Placement = pos=(0,0,4) rot=(0,0,1;0rad)
  sketch-geometry (16):
    g0: LineSegment StartX=0 StartY=0 StartZ=0 EndX=15.2 EndY=0 EndZ=0
    g1: Circle CenterX=3.71 CenterY=7.45 CenterZ=0 NormalX=0 NormalY=0 NormalZ=1 Radius=2.08
    g2: Circle CenterX=8.8865 CenterY=7.45 CenterZ=0 NormalX=0 NormalY=0 NormalZ=1 Radius=2.08
    g3: Circle CenterX=11.4178 CenterY=3.06406 CenterZ=0 NormalX=0 NormalY=0 NormalZ=1 Radius=2.08
    g4: Circle CenterX=6.22788 CenterY=3.05007 CenterZ=0 NormalX=0 NormalY=0 NormalZ=1 Radius=2.08
    g5: ArcOfCircle CenterX=-1.29213 CenterY=7.49891 CenterZ=0 NormalX=0 NormalY=0 NormalZ=1 Radius=2.27568 StartAngle=5.31622 EndAngle=7.25015
    g6: ArcOfCircle CenterX=1.20105 CenterY=3.06417 CenterZ=0 NormalX=0 NormalY=0 NormalZ=1 Radius=2.08 StartAngle=4.09681 EndAngle=8.46956
    g7: ArcOfCircle CenterX=13.9805 CenterY=7.48824 CenterZ=0 NormalX=0 NormalY=0 NormalZ=1 Radius=2.08 StartAngle=0.944332 EndAngle=5.33885
    g8: LineSegment StartX=15.2 StartY=5.80322 StartZ=0 EndX=15.2 EndY=4.94257 EndZ=0
    g9: LineSegment StartX=15.2 StartY=1.15374 StartZ=0 EndX=15.2 EndY=0 EndZ=0
    g10: LineSegment StartX=0 StartY=0 StartZ=0 EndX=0 EndY=1.36598 EndZ=0
    g11: LineSegment StartX=0 StartY=4.76237 StartZ=0 EndX=0 EndY=5.62564 EndZ=0
    g12: ArcOfCircle CenterX=16.4748 CenterY=3.04816 CenterZ=0 NormalX=0 NormalY=0 NormalZ=1 Radius=2.28338 StartAngle=2.1631 EndAngle=4.12008
    g13: LineSegment StartX=0 StartY=11 StartZ=0 EndX=15.2 EndY=11 EndZ=0
    g14: LineSegment StartX=15.2 StartY=9.17326 StartZ=0 EndX=15.2 EndY=11 EndZ=0
    g15: LineSegment StartX=0 StartY=9.37218 StartZ=0 EndX=0 EndY=11 EndZ=0
  constraints (36):
    c: Horizontal(g0)
    c: Coincident(g0,g-1)
    c: Radius(g1) = 2.08
    c: DistanceY(g-1,g1) = 7.45
    c: DistanceX(g-1,g1) = 3.71
    c: Radius(g2) = 2.08
    c: Radius(g3) = 2.08
    c: Radius(g4) = 2.08
    c: Radius(g6) = 2.08
    c: Radius(g7) = 2.08
    c: DistanceY(g-1,g2) = 7.45
    c: Coincident(g8,g7)
    c: Vertical(g8)
    c: Coincident(g9,g0)
    c: Vertical(g9)
    c: Coincident(g10,g-1)
    c: Coincident(g10,g6)
    c: Vertical(g10)
    c: Coincident(g11,g6)
    c: Coincident(g11,g5)
    c: Vertical(g11)
    c: DistanceX(g5,g7) = 15.2
    c: DistanceX(g-1,g0) = 15.2
    c: Coincident(g12,g8)
    c: Coincident(g12,g9)
    c: DistanceX(g-1,g5) = 0
    c: DistanceX(g-1,g6) = 0
    c: Horizontal(g13)
    c: Coincident(g14,g7)
    c: Coincident(g14,g13)
    c: Vertical(g14)
    c: DistanceY(g-1,g13) = 11
    c: DistanceX(g13,g-1) = 0
    c: Coincident(g15,g5)
    c: Coincident(g15,g13)
    c: DistanceX(g13,g13) = 15.2
FEATURE [PartDesign::Pad] Pad009
  Length = 3.5
  Length2 = 100
  Placement = pos=(0,0,4) rot=(0,0,1;0rad)
  Sketch = -> Sketch009
  Type = 0
FEATURE [Sketcher::SketchObject] Sketch010
  sketch-geometry (24):
    g0: LineSegment StartX=2.37867 StartY=9.53855 StartZ=0 EndX=3.14154 EndY=8.48461 EndZ=0
    g1: LineSegment StartX=3.14154 StartY=8.48461 StartZ=0 EndX=2.60525 EndY=8.03091 EndZ=0
    g2: LineSegment StartX=2.60525 StartY=8.03091 StartZ=0 EndX=1.60386 EndY=8.87946 EndZ=0
    g3: LineSegment StartX=2.37867 StartY=9.53855 StartZ=0 EndX=1.60386 EndY=8.87946 EndZ=0
    g4: LineSegment StartX=6.78436 StartY=8.94076 StartZ=0 EndX=7.81191 EndY=8.04644 EndZ=0
    g5: LineSegment StartX=7.81191 StartY=8.04644 StartZ=0 EndX=8.27871 EndY=8.4965 EndZ=0
    g6: LineSegment StartX=8.27871 StartY=8.4965 StartZ=0 EndX=7.51318 EndY=9.56846 EndZ=0
    g7: LineSegment StartX=7.51318 StartY=9.56846 StartZ=0 EndX=6.78436 EndY=8.94076 EndZ=0
    g8: LineSegment StartX=11.6397 StartY=9.07747 StartZ=0 EndX=12.905 EndY=8.01886 EndZ=0
    g9: LineSegment StartX=12.905 StartY=8.01886 StartZ=0 EndX=13.2996 EndY=8.47427 EndZ=0
    g10: LineSegment StartX=13.2996 StartY=8.47427 StartZ=0 EndX=12.401 EndY=9.69575 EndZ=0
    g11: LineSegment StartX=12.401 StartY=9.69575 StartZ=0 EndX=11.6397 EndY=9.07747 EndZ=0
    g12: LineSegment StartX=12.1046 StartY=1.97636 StartZ=0 EndX=13.3056 EndY=0.90266 EndZ=0
    g13: LineSegment StartX=13.3056 StartY=0.90266 StartZ=0 EndX=13.8986 EndY=1.72895 EndZ=0
    g14: LineSegment StartX=13.8986 StartY=1.72895 StartZ=0 EndX=12.5452 EndY=2.53763 EndZ=0
    g15: LineSegment StartX=12.5452 StartY=2.53763 StartZ=0 EndX=12.1046 EndY=1.97636 EndZ=0
    g16: LineSegment StartX=8.70009 StartY=1.7485 StartZ=0 EndX=7.31743 EndY=2.50872 EndZ=0
    g17: LineSegment StartX=7.31743 StartY=2.50872 StartZ=0 EndX=6.93042 EndY=2.02516 EndZ=0
    g18: LineSegment StartX=6.93042 StartY=2.02516 StartZ=0 EndX=8.13703 EndY=1.0298 EndZ=0
    g19: LineSegment StartX=8.13703 StartY=1.0298 StartZ=0 EndX=8.70009 EndY=1.7485 EndZ=0
    g20: LineSegment StartX=2.27306 StartY=2.56746 StartZ=0 EndX=3.50885 EndY=1.8824 EndZ=0
    g21: LineSegment StartX=3.50885 StartY=1.8824 StartZ=0 EndX=2.89778 EndY=1.21181 EndZ=0
    g22: LineSegment StartX=2.89778 StartY=1.21181 StartZ=0 EndX=1.89388 EndY=2.05588 EndZ=0
    g23: LineSegment StartX=1.89388 StartY=2.05588 StartZ=0 EndX=2.27306 EndY=2.56746 EndZ=0
  constraints (24):
    c: Coincident(g1,g0)
    c: Coincident(g2,g1)
    c: Coincident(g3,g0)
    c: Coincident(g3,g2)
    c: Coincident(g4,g5)
    c: Coincident(g5,g6)
    c: Coincident(g6,g7)
    c: Coincident(g7,g4)
    c: Coincident(g8,g9)
    c: Coincident(g9,g10)
    c: Coincident(g10,g11)
    c: Coincident(g11,g8)
    c: Coincident(g12,g13)
    c: Coincident(g13,g14)
    c: Coincident(g14,g15)
    c: Coincident(g15,g12)
    c: Coincident(g16,g17)
    c: Coincident(g17,g18)
    c: Coincident(g18,g19)
    c: Coincident(g19,g16)
    c: Coincident(g20,g21)
    c: Coincident(g21,g22)
    c: Coincident(g22,g23)
    c: Coincident(g23,g20)
FEATURE [PartDesign::Pad] Pad010
  Length = 3
  Length2 = 100
  Sketch = -> Sketch010
  Type = 0
FEATURE [PartDesign::Chamfer] Chamfer005
  Base = -> Pad008 [Edge14,Edge35]
  Size = 1.16
FEATURE [Part::MultiFuse] Fusion002
  Shapes = -> [Chamfer005,Pad010,Pad009]
FEATURE [Part::Box] Box001  label="Würfel001"
  Height = 10
  Length = 15.2
  Placement = pos=(0,11,2) rot=(0,0,1;0rad)
  Width = 18
FEATURE [Part::Cut] Cut001
  Base = -> Fusion002
  Tool = -> Box001
FEATURE [PartDesign::Fillet] Fillet001
  Base = -> Cut001 [Edge80]
  Radius = 1
FEATURE [Part::MultiFuse] Fusion003  label="MotorHolder_1"
  Placement = pos=(0,-13.4,6.1) rot=(1,0,0;3.14159rad)
  Shapes = -> [Fillet,Cut]
FEATURE [Part::MultiFuse] Fusion004  label="MotorHolder_2"
  Placement = pos=(15.18,-8,6.1) rot=(0,1,0;3.14159rad)
  Shapes = -> [Cut001,Fillet001]
